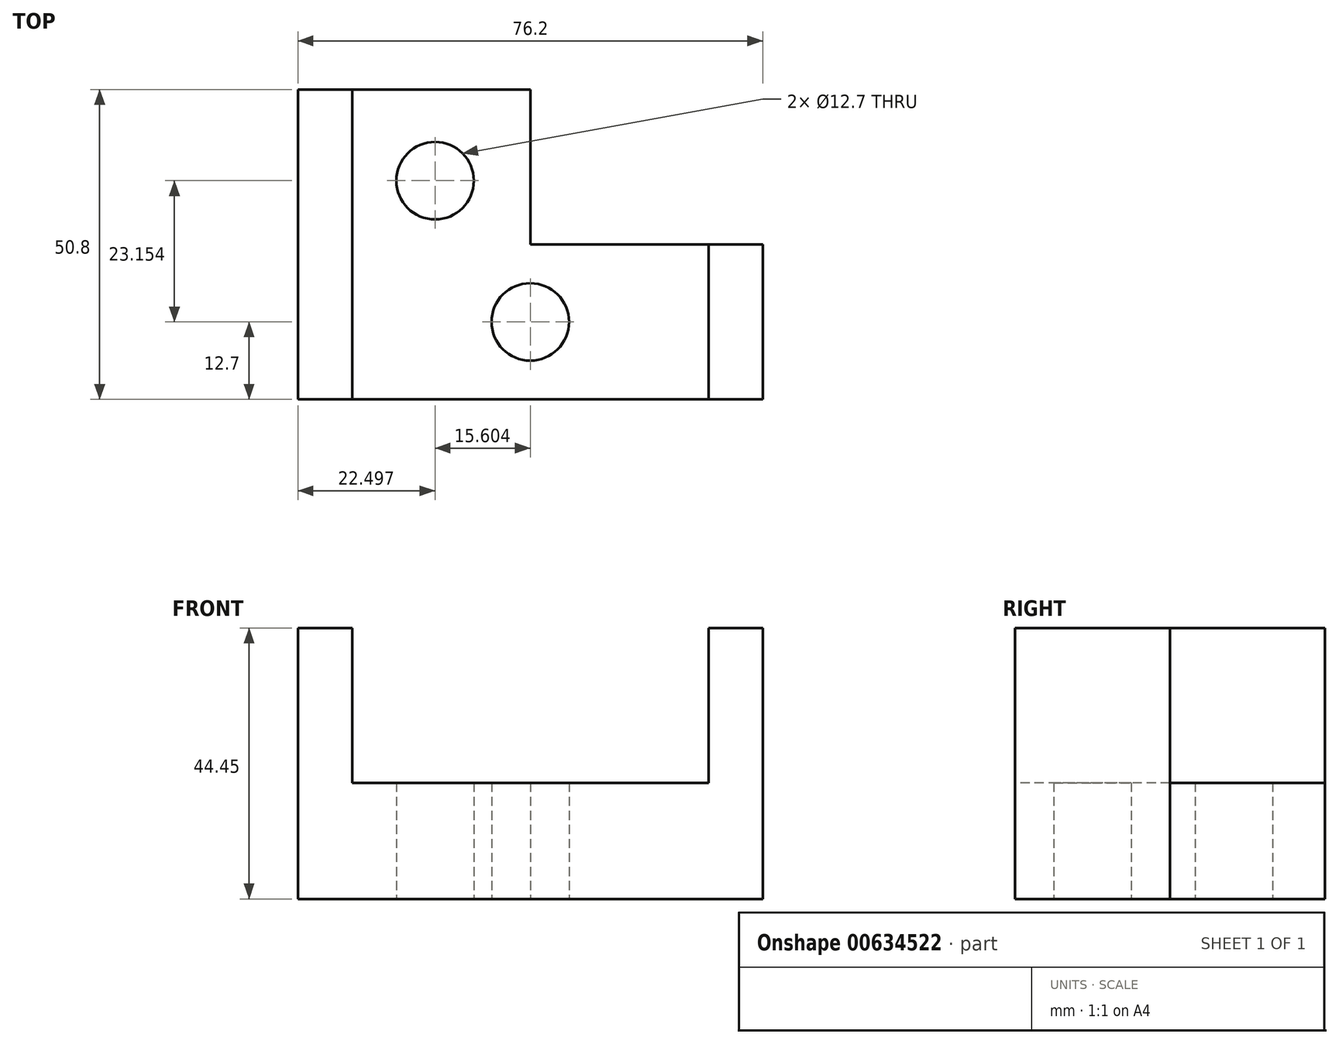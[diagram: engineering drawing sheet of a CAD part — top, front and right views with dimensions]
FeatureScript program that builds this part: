
annotation { "Feature Type Name" : "Feature", "Feature Type Description" : "" }
export const myFeature = defineFeature(function(context is Context, id is Id, definition is map)
    precondition{}
    {
        {
            var Q0;
            Q0=qCreatedBy(makeId("Top.planeOp"),FACE);
            var sketch = newSketch(context, id + "F0", { "sketchPlane" : qUnion([Q0])});
            skLineSegment(sketch, "E0.bottom", {"start": v(38.1, 12.7) * mm, "end": v(0, 12.7) * mm});
            skLineSegment(sketch, "E0.top", {"start": v(38.1, -12.7) * mm, "end": v(-38.1, -12.7) * mm});
            skLineSegment(sketch, "E0.left", {"start": v(38.1, 12.7) * mm, "end": v(38.1, -12.7) * mm});
            skLineSegment(sketch, "E0.right", {"start": v(-38.1, 12.7) * mm, "end": v(-38.1, -12.7) * mm});
            skPoint(sketch, "E0.middle", {"position": v(0, 0) * mm});
            skLineSegment(sketch, "E1.top", {"start": v(-38.1, 38.1) * mm, "end": v(0, 38.1) * mm});
            skLineSegment(sketch, "E1.left", {"start": v(-38.1, 12.7) * mm, "end": v(-38.1, 38.1) * mm});
            skLineSegment(sketch, "E1.right", {"start": v(0, 12.7) * mm, "end": v(0, 38.1) * mm});
            skCircle(sketch, "E2", {"center": v(-15.6, 23.15) * mm, "radius": 6.35 * mm});
            skCircle(sketch, "E3", {"center": v(0, 0) * mm, "radius": 6.35 * mm});
            skSolve(sketch);
        }
        {
            var Q0;
            Q0=makeQuery(id+"F0.imprint","IMPRINT",FACE,{"disambiguationData":[TD([[makeQuery(id+"F0.imprint","IMPRINT",EDGE,{"derivedFrom":sQuery(id+"F0.wireOp",EDGE,"E0.bottom")}),1.0]])]});
            extrude(context, id + "F1", {"entities" : qUnion([Q0]), "depth" : 19.05 * mm, "offsetDistance" : 25.4 * mm});
        }
        {
            var Q0;
            Q0=makeQuery(id+"F1.opExtrude","CAP_FACE",FACE,{"disambiguationData":[OSD([sQuery(id+"F0.wireOp",EDGE,"E0.bottom"),sQuery(id+"F0.wireOp",EDGE,"E0.top"),sQuery(id+"F0.wireOp",EDGE,"E0.left"),sQuery(id+"F0.wireOp",EDGE,"E0.right"),sQuery(id+"F0.wireOp",EDGE,"E1.top"),sQuery(id+"F0.wireOp",EDGE,"E1.left"),sQuery(id+"F0.wireOp",EDGE,"E1.right"),sQuery(id+"F0.wireOp",EDGE,"E2"),sQuery(id+"F0.wireOp",EDGE,"E3")])],"isStart":false});
            var sketch = newSketch(context, id + "F2", { "sketchPlane" : qUnion([Q0])});
            skLineSegment(sketch, "E4.bottom", {"start": v(-38.1, 38.1) * mm, "end": v(-29.21, 38.1) * mm});
            skLineSegment(sketch, "E4.top", {"start": v(-38.1, -12.7) * mm, "end": v(-29.21, -12.7) * mm});
            skLineSegment(sketch, "E4.left", {"start": v(-38.1, 38.1) * mm, "end": v(-38.1, -12.7) * mm});
            skLineSegment(sketch, "E4.right", {"start": v(-29.21, 38.1) * mm, "end": v(-29.21, -12.7) * mm});
            skLineSegment(sketch, "E5.bottom", {"start": v(29.21, 12.7) * mm, "end": v(38.1, 12.7) * mm});
            skLineSegment(sketch, "E5.top", {"start": v(29.21, -12.7) * mm, "end": v(38.1, -12.7) * mm});
            skLineSegment(sketch, "E5.left", {"start": v(29.21, 12.7) * mm, "end": v(29.21, -12.7) * mm});
            skLineSegment(sketch, "E5.right", {"start": v(38.1, 12.7) * mm, "end": v(38.1, -12.7) * mm});
            skSolve(sketch);
        }
        {
            var Q0;
            Q0=makeQuery(id+"F2.imprint","IMPRINT",FACE,{"disambiguationData":[TD([[makeQuery(id+"F2.imprint","IMPRINT",EDGE,{"derivedFrom":sQuery(id+"F2.wireOp",EDGE,"E5.bottom")}),1.0]])]});
            extrude(context, id + "F3", {"entities" : qUnion([Q0]), "operationType" : NewBodyOperationType.ADD, "depth" : 25.4 * mm, "offsetDistance" : 25.4 * mm});
        }
        {
            var Q0;
            Q0 = qSketchRegion(id + "F2", true);
            extrude(context, id + "F4", {"entities" : qUnion([Q0]), "operationType" : NewBodyOperationType.ADD, "depth" : 25.4 * mm, "offsetDistance" : 25.4 * mm});
        }
    });
